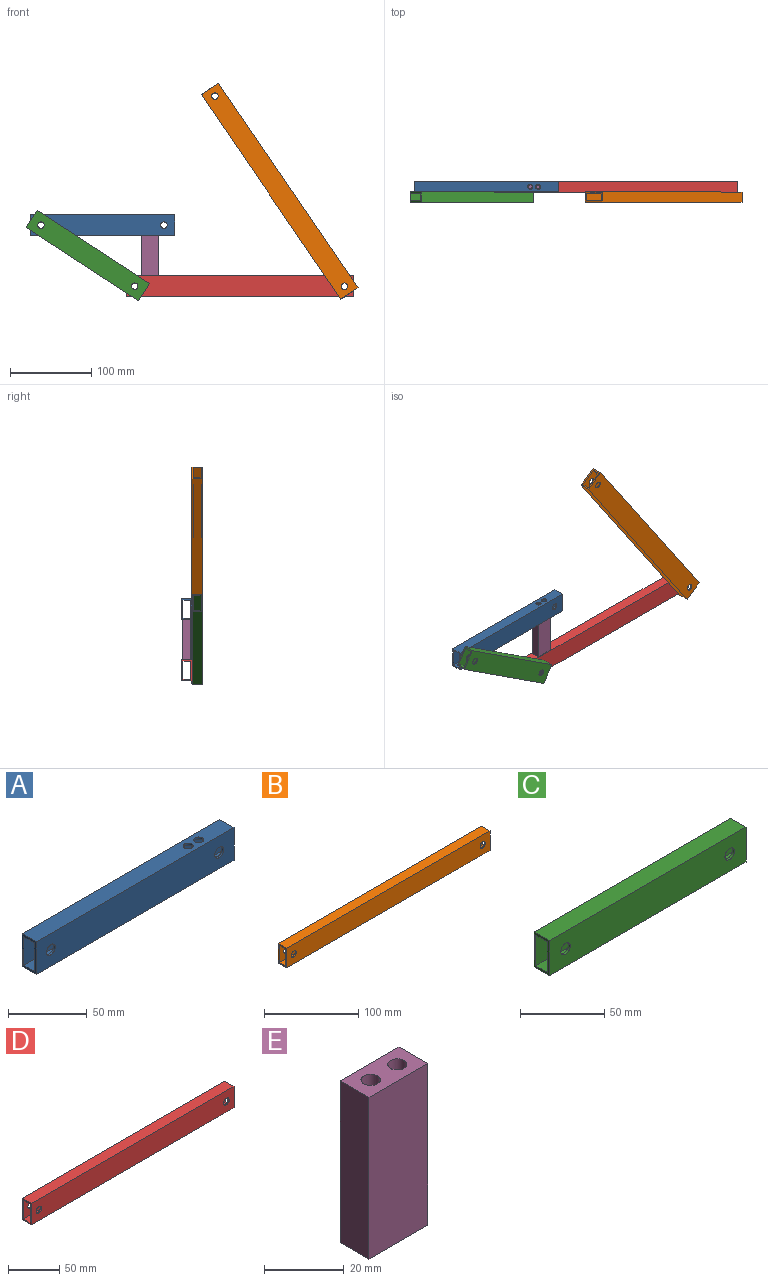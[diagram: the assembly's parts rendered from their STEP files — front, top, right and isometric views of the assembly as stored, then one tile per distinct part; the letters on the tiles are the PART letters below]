
ASSEMBLY  parts=5 mates=5
PART A: 18 faces, bbox 177.8x12.7x25.4 mm
  f0: plane 177.8x12.7mm, normal (0,0,-1), area 2217.5mm2, adj f1,f7,f8,f9,f14,f15
  f1: plane 177.8x25.4mm, normal (0,1,0), area 4417.2mm2, adj f0,f2,f8,f9,f12,f13
  f2: plane 177.8x12.7mm, normal (0,0,1), area 2194.7mm2, adj f1,f7,f8,f9,f16,f17
  f3: plane 177.8x22.23mm, normal (0,-1,0), area 3852.6mm2, adj f4,f6,f8,f9,f12,f13
  f4: plane 177.8x9.53mm, normal (0,0,1), area 1653mm2, adj f3,f5,f8,f9,f14,f15
  f5: plane 177.8x22.23mm, normal (0,1,0), area 3852.6mm2, adj f4,f6,f8,f9,f10,f11
  f6: plane 177.8x9.53mm, normal (0,0,-1), area 1630.2mm2, adj f3,f5,f8,f9,f16,f17
  f7: plane 177.8x25.4mm, normal (0,-1,0), area 4417.2mm2, adj f0,f2,f8,f9,f10,f11
  f8: plane 25.4x12.7mm, normal (1,0,0), area 110.9mm2, adj f0,f1,f2,f3,f4,f5,f6,f7
  f9: plane 25.4x12.7mm, normal (-1,0,0), area 110.9mm2, adj f0,f1,f2,f3,f4,f5,f6,f7
  f10: cylinder r=3.97mm len=7.94mm, axis (0,-1,0), area 39.6mm2, adj f5,f7
  f11: cylinder r=3.97mm len=7.94mm, axis (0,-1,0), area 39.6mm2, adj f5,f7
  f12: cylinder r=3.97mm len=7.94mm, axis (0,-1,0), area 39.6mm2, adj f1,f3
  f13: cylinder r=3.97mm len=7.94mm, axis (0,-1,0), area 39.6mm2, adj f1,f3
  f14: cylinder r=2.54mm len=5.08mm, axis (0,0,1), area 25.3mm2, adj f0,f4
  f15: cylinder r=2.54mm len=5.08mm, axis (0,0,1), area 25.3mm2, adj f0,f4
  f16: cylinder r=3.17mm len=6.35mm, axis (0,0,1), area 31.7mm2, adj f2,f6
  f17: cylinder r=3.17mm len=6.35mm, axis (0,0,1), area 31.7mm2, adj f2,f6
PART B: 14 faces, bbox 304.8x12.7x25.4 mm
  f0: plane 304.8x12.7mm, normal (0,0,-1), area 3871mm2, adj f1,f7,f8,f9
  f1: plane 304.8x25.4mm, normal (0,1,0), area 7643mm2, adj f0,f2,f8,f9,f12,f13
  f2: plane 304.8x12.7mm, normal (0,0,1), area 3871mm2, adj f1,f7,f8,f9
  f3: plane 304.8x22.23mm, normal (0,-1,0), area 6675.2mm2, adj f4,f6,f8,f9,f12,f13
  f4: plane 304.8x9.53mm, normal (0,0,1), area 2903.2mm2, adj f3,f5,f8,f9
  f5: plane 304.8x22.23mm, normal (0,1,0), area 6675.2mm2, adj f4,f6,f8,f9,f10,f11
  f6: plane 304.8x9.53mm, normal (0,0,-1), area 2903.2mm2, adj f3,f5,f8,f9
  f7: plane 304.8x25.4mm, normal (0,-1,0), area 7643mm2, adj f0,f2,f8,f9,f10,f11
  f8: plane 25.4x12.7mm, normal (1,0,0), area 110.9mm2, adj f0,f1,f2,f3,f4,f5,f6,f7
  f9: plane 25.4x12.7mm, normal (-1,0,0), area 110.9mm2, adj f0,f1,f2,f3,f4,f5,f6,f7
  f10: cylinder r=3.97mm len=7.94mm, axis (0,-1,0), area 39.6mm2, adj f5,f7
  f11: cylinder r=3.97mm len=7.94mm, axis (0,-1,0), area 39.6mm2, adj f5,f7
  f12: cylinder r=3.97mm len=7.94mm, axis (0,-1,0), area 39.6mm2, adj f1,f3
  f13: cylinder r=3.97mm len=7.94mm, axis (0,-1,0), area 39.6mm2, adj f1,f3
PART C: 14 faces, bbox 165.1x12.7x25.4 mm
  f0: plane 165.1x12.7mm, normal (0,0,-1), area 2096.8mm2, adj f1,f7,f8,f9
  f1: plane 165.1x25.4mm, normal (0,1,0), area 4094.6mm2, adj f0,f2,f8,f9,f12,f13
  f2: plane 165.1x12.7mm, normal (0,0,1), area 2096.8mm2, adj f1,f7,f8,f9
  f3: plane 165.1x22.23mm, normal (0,-1,0), area 3570.4mm2, adj f4,f6,f8,f9,f12,f13
  f4: plane 165.1x9.53mm, normal (0,0,1), area 1572.6mm2, adj f3,f5,f8,f9
  f5: plane 165.1x22.23mm, normal (0,1,0), area 3570.4mm2, adj f4,f6,f8,f9,f10,f11
  f6: plane 165.1x9.53mm, normal (0,0,-1), area 1572.6mm2, adj f3,f5,f8,f9
  f7: plane 165.1x25.4mm, normal (0,-1,0), area 4094.6mm2, adj f0,f2,f8,f9,f10,f11
  f8: plane 25.4x12.7mm, normal (1,0,0), area 110.9mm2, adj f0,f1,f2,f3,f4,f5,f6,f7
  f9: plane 25.4x12.7mm, normal (-1,0,0), area 110.9mm2, adj f0,f1,f2,f3,f4,f5,f6,f7
  f10: cylinder r=3.97mm len=7.94mm, axis (0,-1,0), area 39.6mm2, adj f5,f7
  f11: cylinder r=3.97mm len=7.94mm, axis (0,-1,0), area 39.6mm2, adj f5,f7
  f12: cylinder r=3.97mm len=7.94mm, axis (0,-1,0), area 39.6mm2, adj f1,f3
  f13: cylinder r=3.97mm len=7.94mm, axis (0,-1,0), area 39.6mm2, adj f1,f3
PART D: 14 faces, bbox 279.4x12.7x25.4 mm
  f0: plane 279.4x22.23mm, normal (0,-1,0), area 6110.7mm2, adj f1,f7,f8,f9,f12,f13
  f1: plane 279.4x9.54mm, normal (0,0,1), area 2664.1mm2, adj f0,f2,f8,f9
  f2: plane 279.4x22.23mm, normal (0,1,0), area 6110.7mm2, adj f1,f7,f8,f9,f10,f11
  f3: plane 279.4x25.4mm, normal (0,1,0), area 6997.8mm2, adj f4,f6,f8,f9,f12,f13
  f4: plane 279.4x12.7mm, normal (0,0,1), area 3548.4mm2, adj f3,f5,f8,f9
  f5: plane 279.4x25.4mm, normal (0,-1,0), area 6997.8mm2, adj f4,f6,f8,f9,f10,f11
  f6: plane 279.4x12.7mm, normal (0,0,-1), area 3548.4mm2, adj f3,f5,f8,f9
  f7: plane 279.4x9.54mm, normal (0,0,-1), area 2664.1mm2, adj f0,f2,f8,f9
  f8: plane 25.4x12.7mm, normal (1,0,0), area 110.7mm2, adj f0,f1,f2,f3,f4,f5,f6,f7
  f9: plane 25.4x12.7mm, normal (-1,0,0), area 110.7mm2, adj f0,f1,f2,f3,f4,f5,f6,f7
  f10: cylinder r=3.97mm len=7.94mm, axis (0,-1,0), area 39.5mm2, adj f2,f5
  f11: cylinder r=3.97mm len=7.94mm, axis (0,-1,0), area 39.5mm2, adj f2,f5
  f12: cylinder r=3.97mm len=7.94mm, axis (0,-1,0), area 39.5mm2, adj f0,f3
  f13: cylinder r=3.97mm len=7.94mm, axis (0,-1,0), area 39.5mm2, adj f0,f3
PART E: 10 faces, bbox 20.8x10.2x49.8 mm
  f0: plane 49.76x20.83mm, normal (0,-1,0), area 1036.4mm2, adj f1,f3,f4,f5
  f1: plane 49.76x10.16mm, normal (1,0,0), area 505.5mm2, adj f0,f2,f4,f5
  f2: plane 49.76x20.83mm, normal (0,1,0), area 1036.4mm2, adj f1,f3,f4,f5
  f3: plane 49.76x10.16mm, normal (-1,0,0), area 505.5mm2, adj f0,f2,f4,f5
  f4: plane 20.83x10.16mm, normal (0,0,1), area 175mm2, adj f0,f1,f2,f3,f6,f8
  f5: plane 20.83x10.16mm, normal (0,0,-1), area 211.6mm2, adj f0,f1,f2,f3
  f6: cylinder r=2.41mm len=19.05mm, axis (0,0,1), area 288.8mm2, adj f4,f7
  f7: plane 4.83x4.83mm, normal (0,0,1), area 18.3mm2, adj f6
  f8: cylinder r=2.41mm len=19.05mm, axis (0,0,1), area 288.8mm2, adj f4,f9
  f9: plane 4.83x4.83mm, normal (0,0,1), area 18.3mm2, adj f8
PLACE A rot(axis=(0,-1,0),0deg) t=(-163.64,0,-2.92)mm
PLACE B rot(axis=(0,1,0),55.7deg) t=(54.51,-12.7,135.54)mm
PLACE C rot(axis=(0,-1,0),146.9deg) t=(-150.63,-12.7,103.77)mm
PLACE D t=(5.14,0,72.98)mm fixed
PLACE E t=(-43.88,-38.41,56.22)mm
MATE fastened E.f8 <-> A.f14  axis (0,0,1) through (-109.67,0,81.1)mm
MATE revolute D.f10 <-> B.f10  axis (0,-1,0) through (134.25,-6.35,18.64)mm
MATE revolute A.f11 <-> C.f10  axis (0,-1,0) through (-239.28,-6.35,93.8)mm
MATE revolute C.f11 <-> D.f11  axis (0,1,0) through (-123.97,-6.35,18.64)mm
MATE parallel E.f5 <-> D.f4  axis (0,0,-1) through (-104.9,0,31.34)mm
